# Revit family: Diverter_Tub_Spout-Grohe-Lineare-13382_Series
name_source: partatom
category: Plumbing Fixtures
revit_build: Autodesk Revit 2018 (Build: 20170223_1515(x64)
units: mm (PartAtom-declared; Revit-internal decimal feet)

## family parameters
Cut with Voids When Loaded = No
Host = Face
OmniClass Number = 23.45.05.14.21.11
OmniClass Title = Bath/Shower Units
Part Type = Normal
Room Calculation Point = No
Round Connector Dimension = Use Diameter
Shared = Yes

## types (2) — shared parameters
Assembly Code = D2020300
CWFU = 3
Default Elevation = 21"
Description = Lineare Diverter Tub Spout with 4 7⁄16 inch spout reach, pull diverter activated and SlipFit installation.
HWFU = 3
Height = 2 5/8"
IAPMO Compliance = ASME A112.18.1/CSA B125.1
Installation Type = Wall Mounted
Length = 5 13/16"
Manufacturer = Grohe
Price = Prices may vary. Please consult Manufacturer Representative for most up-to-date price list.
Product Documentation Link = https://americanstandard.box.com
Product Page URL = https://www.grohe.us
Revised Date = 07/17/2021
Spout Reach = 4 7/16"
Tempered Water Connection = Yes
Tempered Water Connection Diameter = 5/8"
URL = https://www.grohe.us
Vent Connection = No
WFU = 4
Waste Connection = No
Width = 2 5/8"

## per-type parameters (varying)
| type | Finish | Material |
| 13382001 | Metal-Grohe-001-StarLight Chrome | Metal-Grohe-001-StarLight Chrome |
| 13382EN1 | Metal-Grohe-EN1-Brushed Nickel Infinity Finish | Metal-Grohe-EN1-Brushed Nickel Infinity Finish |

note: column(s) folded — value = type name in every type: Model

## geometry (parser evidence)
native form markers: Sweep x3
no freeform markers — native parametric forms only
